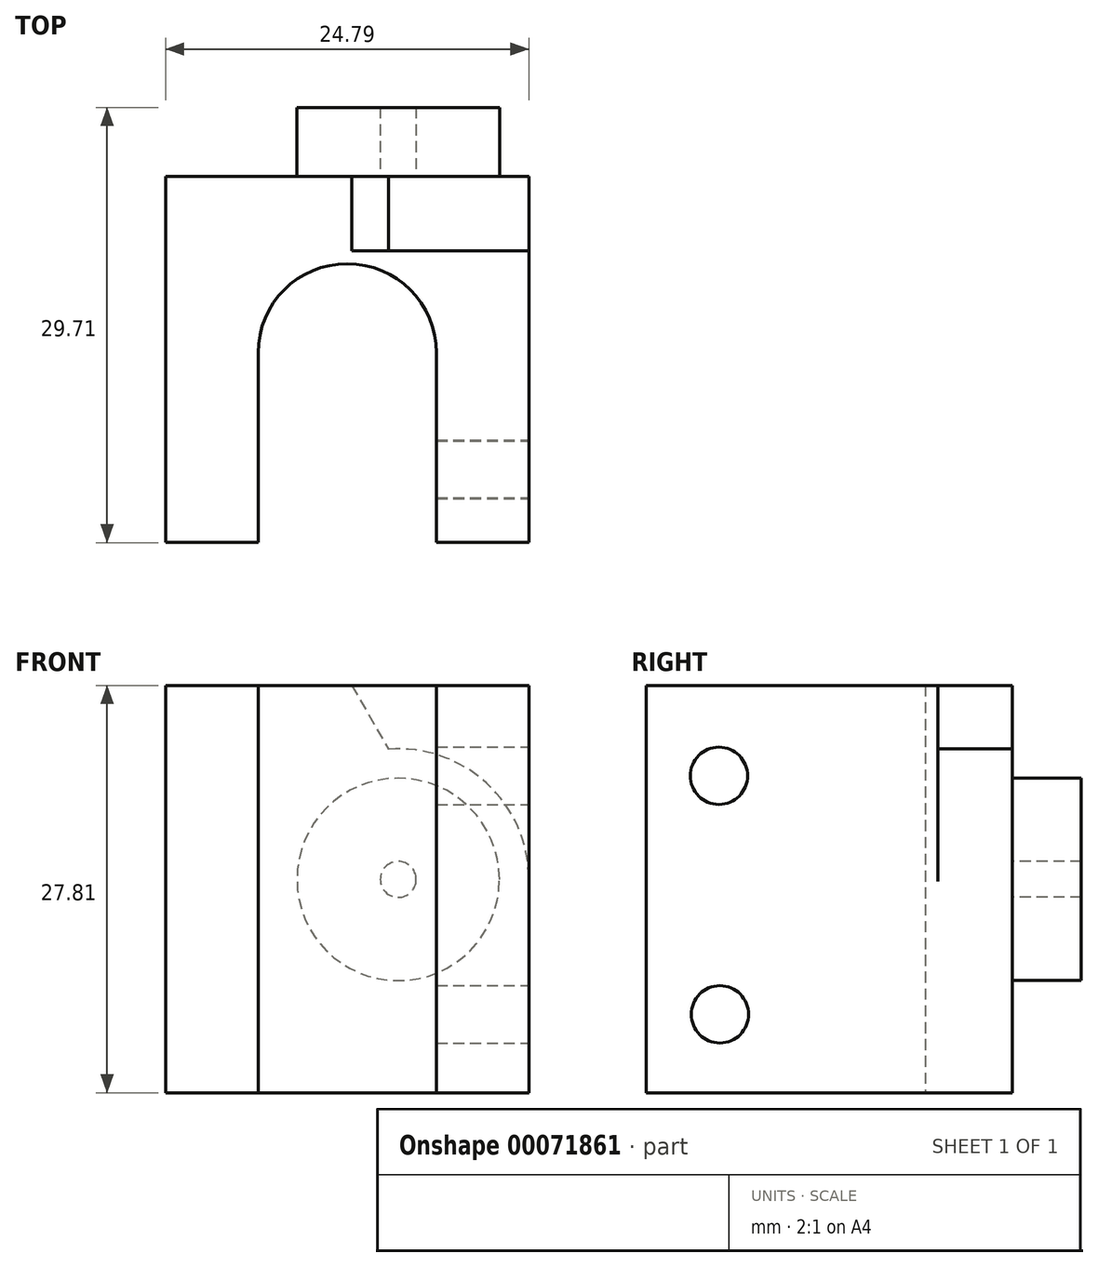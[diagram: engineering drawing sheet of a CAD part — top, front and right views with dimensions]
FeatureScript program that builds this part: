
annotation { "Feature Type Name" : "Feature", "Feature Type Description" : "" }
export const myFeature = defineFeature(function(context is Context, id is Id, definition is map)
    precondition{}
    {
        {
            var Q0;
            Q0=qCreatedBy(makeId("Top.planeOp"),FACE);
            var sketch = newSketch(context, id + "F0", { "sketchPlane" : qUnion([Q0])});
            skLineSegment(sketch, "E0", {"start": v(-18.8, -14.84) * mm, "end": v(-18.8, 10.17) * mm});
            skLineSegment(sketch, "E1", {"start": v(-18.8, 10.17) * mm, "end": v(5.99, 10.17) * mm});
            skLineSegment(sketch, "E2", {"start": v(5.99, 10.17) * mm, "end": v(5.99, -14.84) * mm});
            skLineSegment(sketch, "E3", {"start": v(5.99, -14.84) * mm, "end": v(-0.32, -14.84) * mm});
            skLineSegment(sketch, "E4", {"start": v(-0.32, -14.84) * mm, "end": v(-0.32, -1.88) * mm});
            skLineSegment(sketch, "E5", {"start": v(-12.5, -1.88) * mm, "end": v(-12.5, -14.84) * mm});
            skLineSegment(sketch, "E6", {"start": v(-12.5, -14.84) * mm, "end": v(-18.8, -14.84) * mm});
            skArc(sketch, "E7", {"start": v(-12.5, -1.88) * mm, "mid": v(-6.4, 4.2) * mm, "end": v(-0.32, -1.88) * mm});
            skSolve(sketch);
        }
        {
            var Q0;
            Q0=makeQuery(id+"F0.imprint","IMPRINT",FACE,{"disambiguationData":[TD([[makeQuery(id+"F0.imprint","IMPRINT",EDGE,{"derivedFrom":sQuery(id+"F0.wireOp",EDGE,"E0")}),-1.0]])]});
            extrude(context, id + "F1", {"entities" : qUnion([Q0]), "depth" : 27.8 * mm});
        }
        {
            var Q0;
            Q0=makeQuery(id+"F1.opExtrude","SWEPT_FACE",FACE,{"disambiguationData":[OSD([sQuery(id+"F0.wireOp",EDGE,"E2")])]});
            var sketch = newSketch(context, id + "F2", { "sketchPlane" : qUnion([Q0])});
            skLineSegment(sketch, "E8", {"start": v(-14.84, 30.72) * mm, "end": v(-11.83, 30.72) * mm});
            skLineSegment(sketch, "E9", {"start": v(-11.83, 30.72) * mm, "end": v(-7.91, 30.72) * mm});
            skLineSegment(sketch, "E10", {"start": v(-9.87, 30.72) * mm, "end": v(-9.87, -11.8) * mm});
            skLineSegment(sketch, "E11", {"start": v(-18.08, 27.81) * mm, "end": v(-18.08, 23.6) * mm});
            skLineSegment(sketch, "E12", {"start": v(-18.08, 23.6) * mm, "end": v(-18.08, 19.69) * mm});
            skLineSegment(sketch, "E13", {"start": v(-18.08, 19.69) * mm, "end": v(-18.08, 7.44) * mm});
            skLineSegment(sketch, "E14", {"start": v(-18.08, 7.44) * mm, "end": v(-18.08, 3.53) * mm});
            skLineSegment(sketch, "E15", {"start": v(-18.08, 21.64) * mm, "end": v(-9.87, 21.64) * mm});
            skLineSegment(sketch, "E16", {"start": v(-18.08, 5.49) * mm, "end": v(-9.87, 5.49) * mm});
            skCircle(sketch, "E17", {"center": v(-9.87, 21.64) * mm, "radius": 1.96 * mm});
            skCircle(sketch, "E18", {"center": v(-9.8, 5.35) * mm, "radius": 1.96 * mm});
            skSolve(sketch);
        }
        {
            var Q0;
            {var subQ0=sQuery(id+"F2.wireOp",EDGE,"E10");var subQ1=makeQuery(id+"F2.imprint","INTERSECT",VERTEX,{"derivedFrom":[subQ0,sQuery(id+"F2.wireOp",EDGE,"E15")]});Q0=makeQuery(id+"F2.imprint","IMPRINT",FACE,{"disambiguationData":[TD([[makeQuery(id+"F2.imprint","IMPRINT",EDGE,{"disambiguationData":[TD([[subQ1,1.0]])],"derivedFrom":subQ0}),1.0]])]});}
            var Q1;
            {var subQ0=sQuery(id+"F2.wireOp",EDGE,"E15");var subQ1=sQuery(id+"F2.wireOp",EDGE,"E10");var subQ2=makeQuery(id+"F2.imprint","INTERSECT",VERTEX,{"derivedFrom":[subQ1,subQ0]});Q1=makeQuery(id+"F2.imprint","IMPRINT",FACE,{"disambiguationData":[TD([[makeQuery(id+"F2.imprint","IMPRINT",EDGE,{"disambiguationData":[TD([[subQ2,1.0]])],"derivedFrom":subQ1}),-1.0]])]});}
            var Q2;
            {var subQ0=sQuery(id+"F2.wireOp",EDGE,"E15");var subQ1=sQuery(id+"F2.wireOp",EDGE,"E10");var subQ2=makeQuery(id+"F2.imprint","INTERSECT",VERTEX,{"derivedFrom":[subQ1,subQ0]});Q2=makeQuery(id+"F2.imprint","IMPRINT",FACE,{"disambiguationData":[TD([[makeQuery(id+"F2.imprint","IMPRINT",EDGE,{"disambiguationData":[TD([[subQ2,-1.0]])],"derivedFrom":subQ1}),-1.0]])]});}
            var Q3;
            {var subQ0=sQuery(id+"F2.wireOp",EDGE,"E10");var subQ1=makeQuery(id+"F2.imprint","INTERSECT",VERTEX,{"derivedFrom":[subQ0,sQuery(id+"F2.wireOp",EDGE,"E16")]});Q3=makeQuery(id+"F2.imprint","IMPRINT",FACE,{"disambiguationData":[TD([[makeQuery(id+"F2.imprint","IMPRINT",EDGE,{"disambiguationData":[TD([[subQ1,1.0]])],"derivedFrom":subQ0}),1.0]])]});}
            var Q4;
            {var subQ0=sQuery(id+"F2.wireOp",EDGE,"E16");var subQ1=sQuery(id+"F2.wireOp",EDGE,"E10");var subQ2=makeQuery(id+"F2.imprint","INTERSECT",VERTEX,{"derivedFrom":[subQ1,subQ0]});Q4=makeQuery(id+"F2.imprint","IMPRINT",FACE,{"disambiguationData":[TD([[makeQuery(id+"F2.imprint","IMPRINT",EDGE,{"disambiguationData":[TD([[subQ2,1.0]])],"derivedFrom":subQ1}),-1.0]])]});}
            var Q5;
            {var subQ0=sQuery(id+"F2.wireOp",EDGE,"E16");var subQ1=sQuery(id+"F2.wireOp",EDGE,"E10");var subQ2=makeQuery(id+"F2.imprint","INTERSECT",VERTEX,{"derivedFrom":[subQ1,subQ0]});Q5=makeQuery(id+"F2.imprint","IMPRINT",FACE,{"disambiguationData":[TD([[makeQuery(id+"F2.imprint","IMPRINT",EDGE,{"disambiguationData":[TD([[subQ2,-1.0]])],"derivedFrom":subQ1}),-1.0]])]});}
            extrude(context, id + "F3", {"entities" : qUnion([Q0, Q1, Q2, Q3, Q4, Q5]), "operationType" : NewBodyOperationType.REMOVE, "endBound" : BoundingType.UP_TO_NEXT, "oppositeDirection" : true, "depth" : 25.4 * mm});
        }
        {
            var Q0;
            Q0=makeQuery(id+"F1.opExtrude","SWEPT_FACE",FACE,{"disambiguationData":[OSD([sQuery(id+"F0.wireOp",EDGE,"E1")])]});
            var sketch = newSketch(context, id + "F4", { "sketchPlane" : qUnion([Q0])});
            skLineSegment(sketch, "E19", {"start": v(-5.99, -7.53) * mm, "end": v(9.84, -7.53) * mm});
            skLineSegment(sketch, "E20", {"start": v(9.84, -13.37) * mm, "end": v(-3.98, -13.37) * mm});
            skLineSegment(sketch, "E21", {"start": v(2.93, -13.37) * mm, "end": v(2.93, 21.2) * mm});
            skLineSegment(sketch, "E22", {"start": v(-11.97, 27.81) * mm, "end": v(-11.97, 7.66) * mm});
            skLineSegment(sketch, "E23", {"start": v(-16.07, 7.66) * mm, "end": v(-16.07, 21.48) * mm});
            skLineSegment(sketch, "E24", {"start": v(-16.07, 14.57) * mm, "end": v(2.93, 14.57) * mm});
            skCircle(sketch, "E25", {"center": v(2.93, 14.57) * mm, "radius": 6.9 * mm});
            skCircle(sketch, "E26", {"center": v(2.93, 14.57) * mm, "radius": 1.23 * mm});
            skSolve(sketch);
        }
        {
            var Q0;
            Q0 = qSketchRegion(id + "F4", true);
            extrude(context, id + "F5", {"entities" : qUnion([Q0]), "operationType" : NewBodyOperationType.ADD, "depth" : 4.7 * mm});
        }
        {
            var Q0;
            {var subQ6=sQuery(id+"F0.wireOp",EDGE,"E1");var subQ7=sQuery(id+"F0.wireOp",EDGE,"E0");Q0=makeQuery(id+"F5.boolean.opBoolean","SPLIT",FACE,{"disambiguationData":[TD([makeQuery(id+"F1.opExtrude","SWEPT_FACE",FACE,{"disambiguationData":[OSD([subQ7])]})])],"derivedFrom":makeQuery(id+"F1.opExtrude","SWEPT_FACE",FACE,{"disambiguationData":[OSD([subQ6])]})});}
            var sketch = newSketch(context, id + "F6", { "sketchPlane" : qUnion([Q0])});
            skLineSegment(sketch, "E27", {"start": v(18.8, 35.95) * mm, "end": v(6.1, 35.95) * mm});
            skLineSegment(sketch, "E28", {"start": v(6.1, 35.95) * mm, "end": v(6.1, 27.81) * mm});
            skLineSegment(sketch, "E29", {"start": v(6.1, 27.81) * mm, "end": v(3.59, 23.46) * mm});
            skArc(sketch, "E30", {"start": v(3.59, 23.46) * mm, "mid": v(-3.11, 21.12) * mm, "end": v(-5.99, 14.64) * mm});
            skLineSegment(sketch, "E31", {"start": v(-5.99, 14.64) * mm, "end": v(-5.99, 14.45) * mm});
            skSolve(sketch);
        }
        {
            var Q0;
            Q0 = qSketchRegion(id + "F6", true);
            var Q1;
            {var subQ5=sQuery(id+"F6.wireOp",EDGE,"E29");Q1=makeQuery(id+"F6.imprint","IMPRINT",FACE,{"disambiguationData":[TD([[makeQuery(id+"F6.imprint","IMPRINT",EDGE,{"derivedFrom":subQ5}),-1.0]])]});}
            extrude(context, id + "F7", {"entities" : qUnion([Q0, Q1]), "operationType" : NewBodyOperationType.REMOVE, "oppositeDirection" : true, "depth" : 5.08 * mm});
        }
    });
